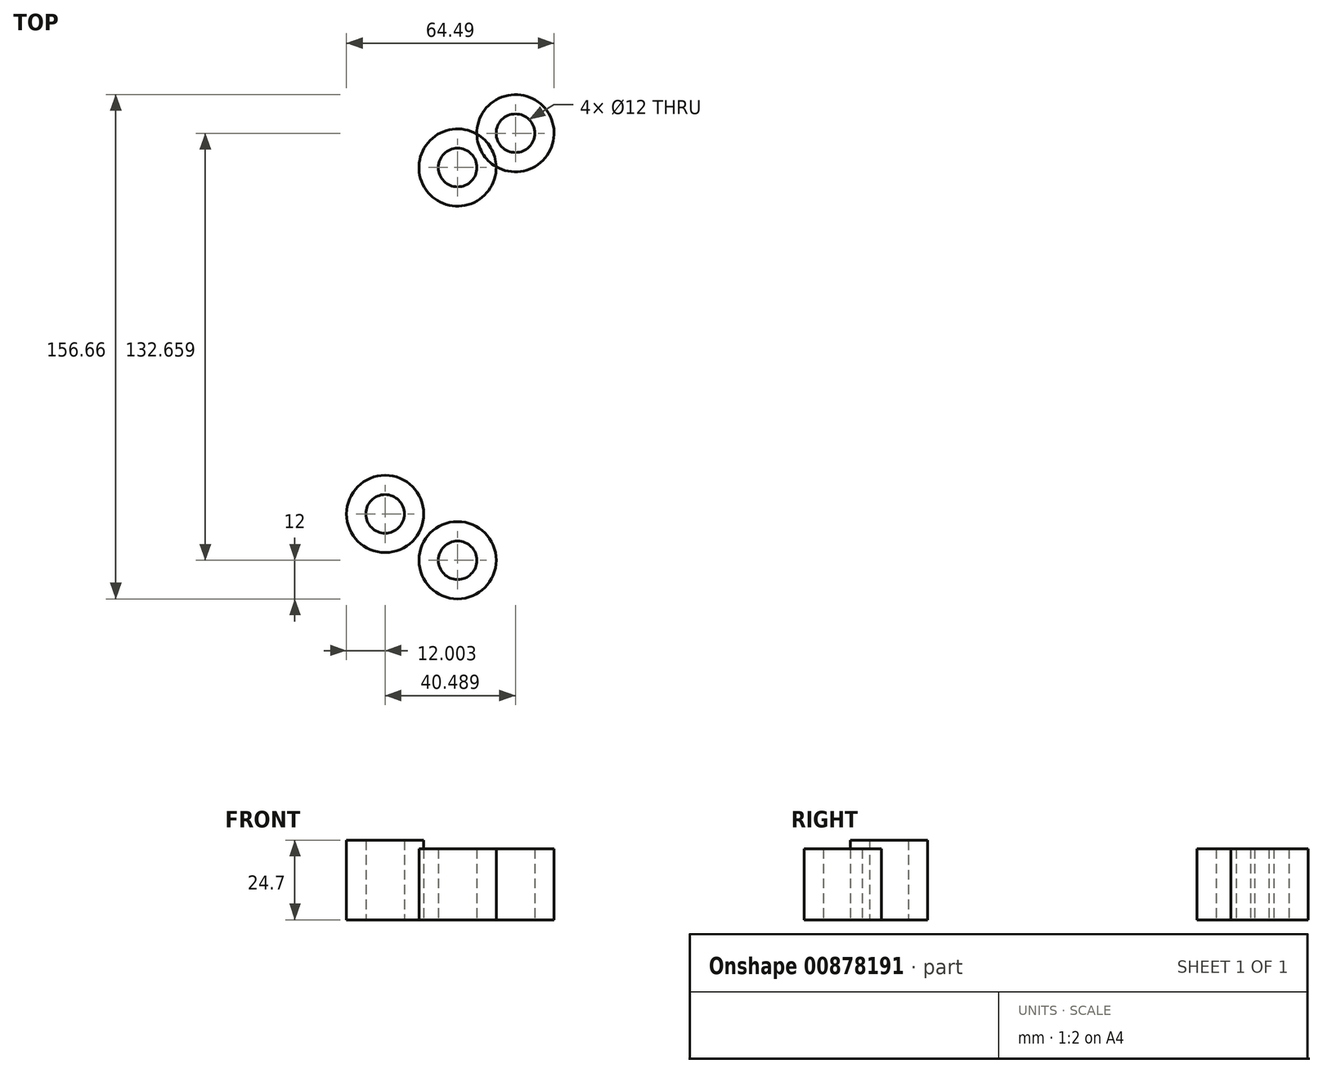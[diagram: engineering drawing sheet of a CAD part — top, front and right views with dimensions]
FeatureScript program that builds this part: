
annotation { "Feature Type Name" : "Feature", "Feature Type Description" : "" }
export const myFeature = defineFeature(function(context is Context, id is Id, definition is map)
    precondition{}
    {
        {
            var Q0;
            Q0=qCreatedBy(makeId("Top.planeOp"),FACE);
            var sketch = newSketch(context, id + "F0", { "sketchPlane" : qUnion([Q0])});
            skCircle(sketch, "E0", {"center": v(0, 0) * mm, "radius": 73.5 * mm, "construction": true});
            skCircle(sketch, "E1", {"center": v(0, 0) * mm, "radius": 70 * mm, "construction": true});
            skCircle(sketch, "E2", {"center": v(-34.34, 61) * mm, "radius": 6 * mm});
            skCircle(sketch, "E3", {"center": v(-34.34, -61) * mm, "radius": 6 * mm});
            skCircle(sketch, "E4", {"center": v(-56.84, -46.6) * mm, "radius": 6 * mm});
            skCircle(sketch, "E5", {"center": v(-16.35, 71.66) * mm, "radius": 6 * mm});
            skLineSegment(sketch, "E6", {"start": v(-16.35, 71.66) * mm, "end": v(-56.84, -46.6) * mm, "construction": true});
            skLineSegment(sketch, "E7", {"start": v(-34.34, 61) * mm, "end": v(-34.34, -61) * mm, "construction": true});
            skCircle(sketch, "E8", {"center": v(-56.84, -46.6) * mm, "radius": 12 * mm});
            skCircle(sketch, "E9", {"center": v(-34.34, -61) * mm, "radius": 12 * mm});
            skCircle(sketch, "E10", {"center": v(-16.35, 71.66) * mm, "radius": 12 * mm});
            skCircle(sketch, "E11", {"center": v(-34.34, 61) * mm, "radius": 12 * mm});
            skLineSegment(sketch, "E12", {"start": v(-34.34, -61) * mm, "end": v(-22.34, -61) * mm});
            skLineSegment(sketch, "E13", {"start": v(-22.34, -61) * mm, "end": v(-22.34, 51.12) * mm});
            skPoint(sketch, "E14.start.orphan", {"position": v(-22.34, 61) * mm});
            skCircle(sketch, "E15", {"center": v(-84.28, -24.88) * mm, "radius": 2.5 * mm});
            skCircle(sketch, "E16", {"center": v(-48.5, 64.2) * mm, "radius": 2.5 * mm});
            skLineSegment(sketch, "E17", {"start": v(-84.28, -24.88) * mm, "end": v(-48.5, 64.2) * mm, "construction": true});
            skLineSegment(sketch, "E18", {"start": v(-56.84, -46.6) * mm, "end": v(-84.28, -24.88) * mm, "construction": true});
            skLineSegment(sketch, "E19", {"start": v(-16.35, 71.66) * mm, "end": v(-48.5, 64.2) * mm, "construction": true});
            skLineSegment(sketch, "E20", {"start": v(-84.28, -24.88) * mm, "end": v(-53.06, -35.57) * mm, "construction": true});
            skLineSegment(sketch, "E21", {"start": v(-48.5, 64.2) * mm, "end": v(-22, 55.14) * mm, "construction": true});
            skCircle(sketch, "E22", {"center": v(-66.39, 19.66) * mm, "radius": 40 * mm, "construction": true});
            skSolve(sketch);
        }
        {
            var Q0;
            Q0=makeQuery(id+"F0.imprint","IMPRINT",FACE,{"disambiguationData":[TD([[makeQuery(id+"F0.imprint","IMPRINT",EDGE,{"derivedFrom":sQuery(id+"F0.wireOp",EDGE,"E2")}),-1.0]])]});
            var Q1;
            Q1=makeQuery(id+"F0.imprint","IMPRINT",FACE,{"disambiguationData":[TD([[makeQuery(id+"F0.imprint","IMPRINT",EDGE,{"derivedFrom":sQuery(id+"F0.wireOp",EDGE,"E3")}),-1.0]])]});
            var Q2;
            {var subQ0=sQuery(id+"F0.wireOp",EDGE,"uvAYMqGV-DIzJ-fmoX-Jquh-CrT9dVzAXWpi");Q2=makeQuery(id+"F0.imprint","IMPRINT",FACE,{"disambiguationData":[TD([[makeQuery(id+"F0.imprint","IMPRINT",EDGE,{"derivedFrom":subQ0}),1.0]])]});}
            var Q3;
            Q3=makeQuery(id+"F0.imprint","IMPRINT",FACE,{"disambiguationData":[TD([[makeQuery(id+"F0.imprint","IMPRINT",EDGE,{"derivedFrom":sQuery(id+"F0.wireOp",EDGE,"E5")}),-1.0]])]});
            var Q4;
            {var subQ0=sQuery(id+"F0.wireOp",EDGE,"5625360e-2d45-4daa-a3da-605d3618f61e.trimOffspring");Q4=makeQuery(id+"F0.imprint","IMPRINT",FACE,{"disambiguationData":[TD([[makeQuery(id+"F0.imprint","IMPRINT",EDGE,{"derivedFrom":subQ0}),1.0]])]});}
            var Q5;
            {var subQ8=sQuery(id+"F0.wireOp",EDGE,"UsUqNIiJ-VfbJ-wgNQ-Aa4I-qdWGud0cX9Ic");Q5=makeQuery(id+"F0.imprint","IMPRINT",FACE,{"disambiguationData":[TD([[makeQuery(id+"F0.imprint","IMPRINT",EDGE,{"derivedFrom":subQ8}),1.0]])]});}
            var Q6;
            {var subQ5=sQuery(id+"F0.wireOp",EDGE,"7202584b-8c20-40f0-bc9d-29dd12e960fb.trimOffspring");Q6=makeQuery(id+"F0.imprint","IMPRINT",FACE,{"disambiguationData":[TD([[makeQuery(id+"F0.imprint","IMPRINT",EDGE,{"derivedFrom":subQ5}),-1.0]])]});}
            extrude(context, id + "F1", {"entities" : qUnion([Q0, Q1, Q2, Q3, Q4, Q5, Q6]), "depth" : 22 * mm, "offsetDistance" : 25 * mm});
        }
        {
            var Q0;
            Q0=makeQuery(id+"F0.imprint","IMPRINT",FACE,{"disambiguationData":[TD([[makeQuery(id+"F0.imprint","IMPRINT",EDGE,{"derivedFrom":sQuery(id+"F0.wireOp",EDGE,"E4")}),-1.0]])]});
            extrude(context, id + "F2", {"entities" : qUnion([Q0]), "operationType" : NewBodyOperationType.ADD, "depth" : 24.7 * mm, "offsetDistance" : 25 * mm});
        }
    });
